# Revit family: Legrand_Enveloppes_industrielles_Metal_Armoires_Atlantic_Version_carree
name_source: partatom
category: Equipement électrique
revit_build: Autodesk Revit 2018 (Build: 20170223_1515(x64)
units: mm (PartAtom-declared; Revit-internal decimal feet)

## family parameters
Basée sur le plan de construction = Non
Configuration du panneau = Deux colonnes, circuits au sein
Cote de connecteur circulaire = Utiliser le diamètre
Couper avec des vides une fois chargée = Non
Numéro OmniClass = 23.80.30.11.17
Partagée = Non
Point de calcul de pièce = Non
Titre OmniClass = Distribution Boards and Control Panels
Toujours verticalement = Oui
Type d'élément = Tableau de raccordement

## types (12) — shared parameters
Conditions Générale d'Utilisation = https://export.legrand.com
ETIM Class 6.0 = EC000058
Fabricant = Legrand
IK = 10
IP = 66
Image du type = Atlantic_carrée_035505_pw_234051_pz_18.jpg
Matière = Polyester
RAL = 7035
URL = www.legrand.fr

## per-type parameters (varying)
| type | Coffret 035505 | Coffret 035510 | Coffret 035515 | Coffret 035520 | Coffret 035524 | Coffret 035530 | Coffret 035531 | Coffret 035532 | Coffret 035536 | Coffret 035591 | Coffret 035594 | Coffret 035597 | Description | Hauteur | Largeur | Poids | distance avant zone d'installation | distance coté zone d'installation | largeur zone d'installation | profondeur | profondeur zone d'installation |
| Legrand_Enveloppes_industrielles_Metal_Armoires_Atlantic_Version_carree 035505 | Oui | Non | Non | Non | Non | Non | Non | Non | Non | Non | Non | Non | Ref 035505 - Legrand_Enveloppes_industrielles_Metal_Armoires_Atlantic_Version_carree | 300 mm | 300 mm | 4.10 kg | 300 mm | 160 mm  [stored 0.524934 ft] | 620 mm | 160 mm  [stored 0.524934 ft] | 460 mm |
| Legrand_Enveloppes_industrielles_Metal_Armoires_Atlantic_Version_carree 035510 | Non | Oui | Non | Non | Non | Non | Non | Non | Non | Non | Non | Non | Ref 035510 - Legrand_Enveloppes_industrielles_Metal_Armoires_Atlantic_Version_carree | 600 mm | 600 mm | 16.30 kg | 600 mm | 250 mm  [stored 0.82021 ft] | 1100 mm | 250 mm  [stored 0.82021 ft] | 850 mm  [stored 2.78871 ft] |
| Legrand_Enveloppes_industrielles_Metal_Armoires_Atlantic_Version_carree 035515 | Non | Non | Oui | Non | Non | Non | Non | Non | Non | Non | Non | Non | Ref 035515 -Legrand_Enveloppes_industrielles_Metal_Armoires_Atlantic_Version_carree | 800 mm  [stored 2.62467 ft] | 800 mm  [stored 2.62467 ft] | 21.60 kg | 800 mm  [stored 2.62467 ft] | 250 mm  [stored 0.82021 ft] | 1300 mm  [stored 4.26509 ft] | 250 mm  [stored 0.82021 ft] | 1050 mm |
| Legrand_Enveloppes_industrielles_Metal_Armoires_Atlantic_Version_carree 035520 | Non | Non | Non | Oui | Non | Non | Non | Non | Non | Non | Non | Non | Ref 035520 - Legrand_Enveloppes_industrielles_Metal_Armoires_Atlantic_Version_carree | 600 mm | 600 mm | 21.10 kg | 600 mm | 300 mm | 1200 mm | 300 mm | 900 mm  [stored 2.95276 ft] |
| Legrand_Enveloppes_industrielles_Metal_Armoires_Atlantic_Version_carree 035524 | Non | Non | Non | Non | Oui | Non | Non | Non | Non | Non | Non | Non | Ref 035524 - Legrand_Enveloppes_industrielles_Metal_Armoires_Atlantic_Version_carree | 800 mm  [stored 2.62467 ft] | 800 mm  [stored 2.62467 ft] | 34.20 kg | 800 mm  [stored 2.62467 ft] | 300 mm | 1400 mm  [stored 4.59318 ft] | 300 mm | 1100 mm |
| Legrand_Enveloppes_industrielles_Metal_Armoires_Atlantic_Version_carree 035530 | Non | Non | Non | Non | Non | Oui | Non | Non | Non | Non | Non | Non | Ref 035530 - Legrand_Enveloppes_industrielles_Metal_Armoires_Atlantic_Version_carree | 300 mm | 300 mm | 4.20 kg | 300 mm | 200 mm  [stored 0.656168 ft] | 700 mm  [stored 2.29659 ft] | 200 mm  [stored 0.656168 ft] | 500 mm  [stored 1.64042 ft] |
| Legrand_Enveloppes_industrielles_Metal_Armoires_Atlantic_Version_carree 035531 | Non | Non | Non | Non | Non | Non | Oui | Non | Non | Non | Non | Non | Ref 035531 - Legrand_Enveloppes_industrielles_Metal_Armoires_Atlantic_Version_carree | 400 mm  [stored 1.31234 ft] | 400 mm  [stored 1.31234 ft] | 7.70 kg | 400 mm  [stored 1.31234 ft] | 200 mm  [stored 0.656168 ft] | 800 mm  [stored 2.62467 ft] | 200 mm  [stored 0.656168 ft] | 600 mm |
| Legrand_Enveloppes_industrielles_Metal_Armoires_Atlantic_Version_carree 035532 | Non | Non | Non | Non | Non | Non | Non | Oui | Non | Non | Non | Non | Ref 035532 - Legrand_Enveloppes_industrielles_Metal_Armoires_Atlantic_Version_carree | 500 mm  [stored 1.64042 ft] | 500 mm  [stored 1.64042 ft] | 11.50 kg | 500 mm  [stored 1.64042 ft] | 250 mm  [stored 0.82021 ft] | 1000 mm  [stored 3.28084 ft] | 250 mm  [stored 0.82021 ft] | 750 mm  [stored 2.46063 ft] |
| Legrand_Enveloppes_industrielles_Metal_Armoires_Atlantic_Version_carree 035536 | Non | Non | Non | Non | Non | Non | Non | Non | Oui | Non | Non | Non | Ref 035536 - Legrand_Enveloppes_industrielles_Metal_Armoires_Atlantic_Version_carree | 600 mm | 600 mm | 28.00 kg | 600 mm | 400 mm  [stored 1.31234 ft] | 1400 mm  [stored 4.59318 ft] | 400 mm  [stored 1.31234 ft] | 1000 mm  [stored 3.28084 ft] |
| Legrand_Enveloppes_industrielles_Metal_Armoires_Atlantic_Version_carree 035591 | Non | Non | Non | Non | Non | Non | Non | Non | Non | Oui | Non | Non | Ref 035591 - Legrand_Enveloppes_industrielles_Metal_Armoires_Atlantic_Version_carree | 1000 mm  [stored 3.28084 ft] | 1000 mm  [stored 3.28084 ft] | 53.00 kg | 1000 mm  [stored 3.28084 ft] | 300 mm | 1600 mm  [stored 5.24934 ft] | 300 mm | 1300 mm  [stored 4.26509 ft] |
| Legrand_Enveloppes_industrielles_Metal_Armoires_Atlantic_Version_carree 035594 | Non | Non | Non | Non | Non | Non | Non | Non | Non | Non | Oui | Non | Ref 035594 - Legrand_Enveloppes_industrielles_Metal_Armoires_Atlantic_Version_carree | 1200 mm | 1200 mm | 70.00 kg | 1200 mm | 300 mm | 1800 mm  [stored 5.90551 ft] | 300 mm | 1500 mm  [stored 4.92126 ft] |
| Legrand_Enveloppes_industrielles_Metal_Armoires_Atlantic_Version_carree 035597 | Non | Non | Non | Non | Non | Non | Non | Non | Non | Non | Non | Oui | Ref 035597 - Legrand_Enveloppes_industrielles_Metal_Armoires_Atlantic_Version_carree | 1200 mm | 1200 mm | 77.00 kg | 1200 mm | 400 mm  [stored 1.31234 ft] | 2000 mm  [stored 6.56168 ft] | 400 mm  [stored 1.31234 ft] | 1600 mm  [stored 5.24934 ft] |

note: [stored X ft] marks values corroborated as IEEE doubles in the binary element streams (Revit-internal decimal feet)
